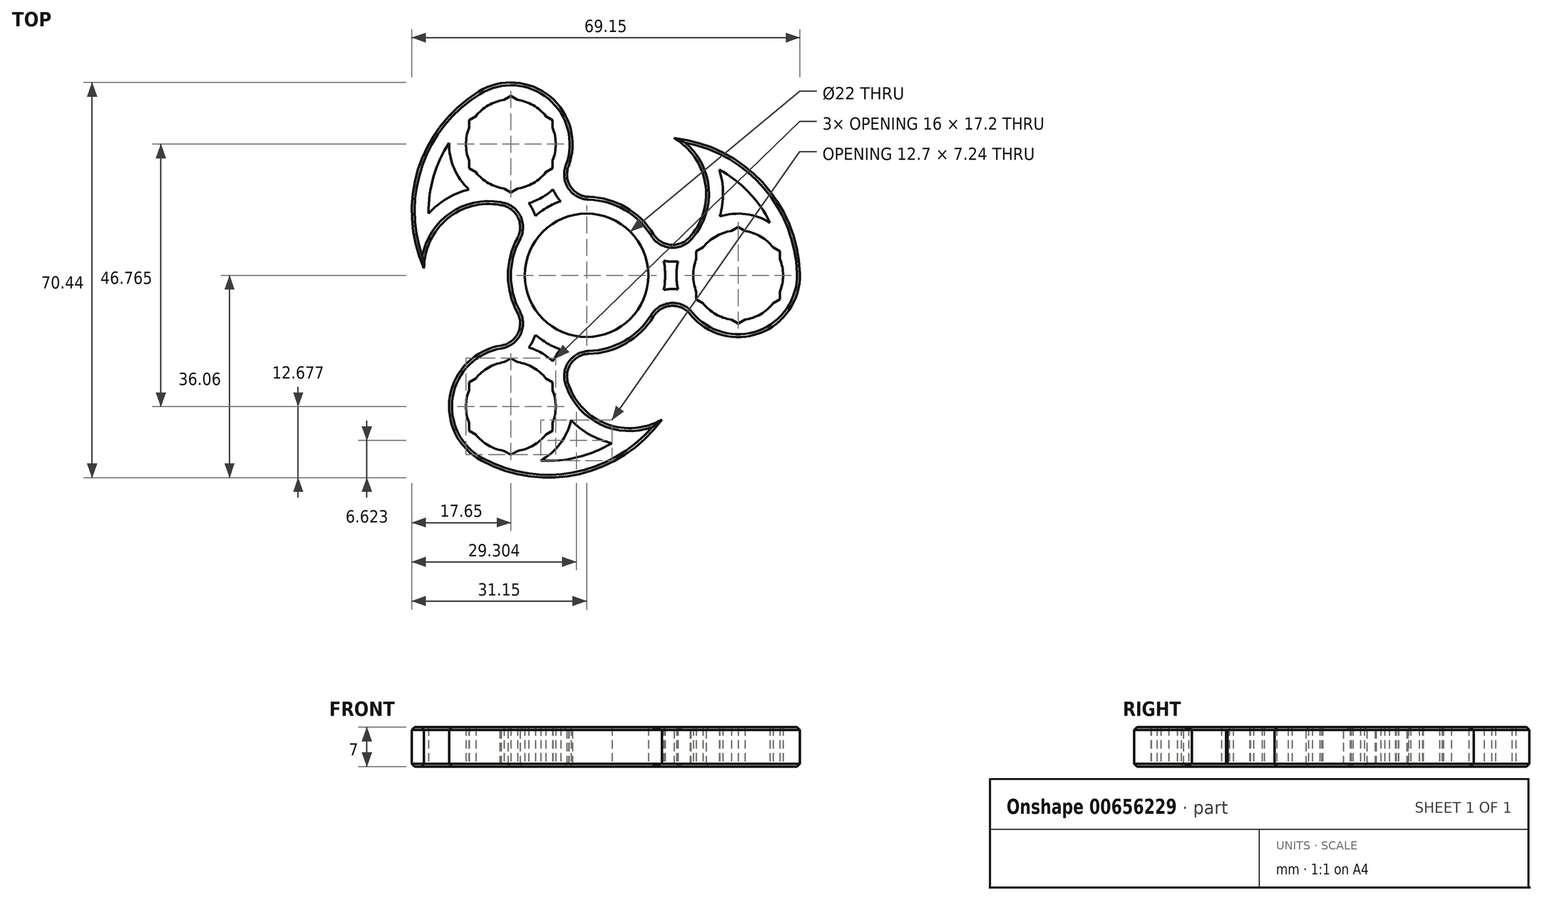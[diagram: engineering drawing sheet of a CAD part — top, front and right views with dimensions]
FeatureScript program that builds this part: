
annotation { "Feature Type Name" : "Feature", "Feature Type Description" : "" }
export const myFeature = defineFeature(function(context is Context, id is Id, definition is map)
    precondition{}
    {
        {
            var Q0;
            Q0=qCreatedBy(makeId("Top.planeOp"),FACE);
            var sketch = newSketch(context, id + "F0", { "sketchPlane" : qUnion([Q0])});
            skCircle(sketch, "E0", {"center": v(0, 0) * mm, "radius": 11 * mm});
            skCircle(sketch, "E1", {"center": v(0, 0) * mm, "radius": 27 * mm, "construction": true});
            skCircle(sketch, "E2", {"center": v(27, 0) * mm, "radius": 8 * mm});
            skArc(sketch, "E3.0", {"start": v(18.44, -6.91) * mm, "mid": v(30.82, -10.32) * mm, "end": v(38, 0.32) * mm});
            skCircle(sketch, "E4", {"center": v(0, 0) * mm, "radius": 29 * mm, "construction": true});
            skLineSegment(sketch, "E5", {"start": v(27, 0) * mm, "end": v(15.57, 24.46) * mm, "construction": true});
            skArc(sketch, "E6", {"start": v(38, 0.32) * mm, "mid": v(31.33, 16.6) * mm, "end": v(15.57, 24.46) * mm});
            skArc(sketch, "E7", {"start": v(18.6, 7.1) * mm, "mid": v(21.14, 16.48) * mm, "end": v(15.57, 24.46) * mm});
            skArc(sketch, "E8.0", {"start": v(13.75, -2.6) * mm, "mid": v(14, 0) * mm, "end": v(13.75, 2.6) * mm});
            skArc(sketch, "E9", {"start": v(11.93, 7.33) * mm, "mid": v(15.08, 5.44) * mm, "end": v(18.44, 6.91) * mm});
            skArc(sketch, "E10.0", {"start": v(13.75, 2.6) * mm, "mid": v(15.02, 2.44) * mm, "end": v(16.29, 2.5) * mm});
            skArc(sketch, "E11.MirrorCS", {"start": v(13.75, -2.6) * mm, "mid": v(15.02, -2.44) * mm, "end": v(16.29, -2.5) * mm});
            skArc(sketch, "E12.MirrorCS", {"start": v(11.93, -7.33) * mm, "mid": v(15.08, -5.44) * mm, "end": v(18.44, -6.91) * mm});
            skArc(sketch, "E13.trimOffspring", {"start": v(16.29, 2.5) * mm, "mid": v(16, 0) * mm, "end": v(16.29, -2.5) * mm});
            skArc(sketch, "E14.trimOffspring", {"start": v(11.93, 7.33) * mm, "mid": v(7, 12.12) * mm, "end": v(0.39, 14) * mm});
            skArc(sketch, "E15.0", {"start": v(32.7, 9.41) * mm, "mid": v(28.89, 14.82) * mm, "end": v(23.64, 18.85) * mm});
            skArc(sketch, "E16.0", {"start": v(23.74, 10.5) * mm, "mid": v(24.3, 14.69) * mm, "end": v(23.64, 18.85) * mm});
            skArc(sketch, "E17.trimOffspring", {"start": v(32.7, 9.41) * mm, "mid": v(28.34, 10.92) * mm, "end": v(23.74, 10.5) * mm});
            skArc(sketch, "E18.1.0", {"start": v(-24.5, 23.6) * mm, "mid": v(-23.62, 19.08) * mm, "end": v(-20.97, 15.3) * mm});
            skArc(sketch, "E18.1.1", {"start": v(-20.97, 15.3) * mm, "mid": v(-24.87, 13.7) * mm, "end": v(-28.15, 11.05) * mm});
            skArc(sketch, "E18.1.2", {"start": v(0.39, 14) * mm, "mid": v(-2.83, 15.77) * mm, "end": v(-3.23, 19.43) * mm});
            skArc(sketch, "E18.1.3", {"start": v(-4.62, 13.22) * mm, "mid": v(-5.4, 14.22) * mm, "end": v(-5.98, 15.35) * mm});
            skArc(sketch, "E18.1.4", {"start": v(-9.14, 10.6) * mm, "mid": v(-9.62, 11.79) * mm, "end": v(-10.3, 12.86) * mm});
            skArc(sketch, "E18.1.5", {"start": v(-12.31, 6.66) * mm, "mid": v(-12.25, 10.34) * mm, "end": v(-15.2, 12.52) * mm});
            skArc(sketch, "E18.1.6", {"start": v(-4.62, 13.22) * mm, "mid": v(-7, 12.12) * mm, "end": v(-9.14, 10.6) * mm});
            skArc(sketch, "E18.1.7", {"start": v(-15.44, 12.56) * mm, "mid": v(-24.84, 10.06) * mm, "end": v(-28.97, 1.26) * mm});
            skArc(sketch, "E18.1.8", {"start": v(-19.27, 32.75) * mm, "mid": v(-30.04, 18.83) * mm, "end": v(-28.97, 1.26) * mm});
            skArc(sketch, "E18.1.9", {"start": v(-3.23, 19.43) * mm, "mid": v(-6.47, 31.85) * mm, "end": v(-19.27, 32.75) * mm});
            skCircle(sketch, "E18.1.10", {"center": v(-13.5, 23.38) * mm, "radius": 8 * mm});
            skArc(sketch, "E18.1.11", {"start": v(-24.5, 23.6) * mm, "mid": v(-27.28, 17.6) * mm, "end": v(-28.15, 11.05) * mm});
            skArc(sketch, "E18.1.12", {"start": v(-10.3, 12.86) * mm, "mid": v(-8, 13.86) * mm, "end": v(-5.98, 15.35) * mm});
            skArc(sketch, "E18.2.0", {"start": v(-8.2, -33.02) * mm, "mid": v(-4.71, -30) * mm, "end": v(-2.77, -25.81) * mm});
            skArc(sketch, "E18.2.1", {"start": v(-2.77, -25.81) * mm, "mid": v(0.57, -28.4) * mm, "end": v(4.5, -29.9) * mm});
            skArc(sketch, "E18.2.2", {"start": v(-12.31, -6.66) * mm, "mid": v(-12.25, -10.34) * mm, "end": v(-15.2, -12.52) * mm});
            skArc(sketch, "E18.2.3", {"start": v(-9.14, -10.6) * mm, "mid": v(-9.62, -11.79) * mm, "end": v(-10.3, -12.86) * mm});
            skArc(sketch, "E18.2.4", {"start": v(-4.62, -13.22) * mm, "mid": v(-5.4, -14.22) * mm, "end": v(-5.98, -15.35) * mm});
            skArc(sketch, "E18.2.5", {"start": v(0.39, -14) * mm, "mid": v(-2.83, -15.77) * mm, "end": v(-3.23, -19.43) * mm});
            skArc(sketch, "E18.2.6", {"start": v(-9.14, -10.6) * mm, "mid": v(-7, -12.12) * mm, "end": v(-4.62, -13.22) * mm});
            skArc(sketch, "E18.2.7", {"start": v(-3.15, -19.65) * mm, "mid": v(3.7, -26.55) * mm, "end": v(13.4, -25.72) * mm});
            skArc(sketch, "E18.2.8", {"start": v(-18.72, -33.06) * mm, "mid": v(-1.28, -35.43) * mm, "end": v(13.4, -25.72) * mm});
            skArc(sketch, "E18.2.9", {"start": v(-15.2, -12.52) * mm, "mid": v(-24.34, -21.53) * mm, "end": v(-18.72, -33.06) * mm});
            skCircle(sketch, "E18.2.10", {"center": v(-13.5, -23.38) * mm, "radius": 8 * mm});
            skArc(sketch, "E18.2.11", {"start": v(-8.2, -33.02) * mm, "mid": v(-1.6, -32.43) * mm, "end": v(4.5, -29.9) * mm});
            skArc(sketch, "E18.2.12", {"start": v(-5.98, -15.35) * mm, "mid": v(-8, -13.86) * mm, "end": v(-10.3, -12.86) * mm});
            skArc(sketch, "E19.trimOffspring", {"start": v(-12.31, 6.66) * mm, "mid": v(-14, 0) * mm, "end": v(-12.31, -6.66) * mm});
            skArc(sketch, "E20.trimOffspring", {"start": v(0.39, -14) * mm, "mid": v(7, -12.12) * mm, "end": v(11.93, -7.33) * mm});
            skLineSegment(sketch, "E21", {"start": v(18.44, 6.91) * mm, "end": v(18.6, 7.1) * mm});
            skLineSegment(sketch, "E22", {"start": v(-15.2, 12.52) * mm, "end": v(-15.44, 12.56) * mm});
            skLineSegment(sketch, "E23", {"start": v(-3.15, -19.65) * mm, "end": v(-3.23, -19.43) * mm});
            skCircle(sketch, "E24.cCircle", {"center": v(27, 0) * mm, "radius": 8.6 * mm, "construction": true});
            skLineSegment(sketch, "E24.0", {"start": v(34.45, 4.3) * mm, "end": v(34.45, -4.3) * mm});
            skLineSegment(sketch, "E24.1", {"start": v(34.45, -4.3) * mm, "end": v(27, -8.6) * mm});
            skLineSegment(sketch, "E24.2", {"start": v(27, -8.6) * mm, "end": v(19.55, -4.3) * mm});
            skLineSegment(sketch, "E24.3", {"start": v(19.55, -4.3) * mm, "end": v(19.55, 4.3) * mm});
            skLineSegment(sketch, "E24.4", {"start": v(19.55, 4.3) * mm, "end": v(27, 8.6) * mm});
            skLineSegment(sketch, "E24.5", {"start": v(27, 8.6) * mm, "end": v(34.45, 4.3) * mm});
            skLineSegment(sketch, "E25.1.0", {"start": v(-13.5, 31.98) * mm, "end": v(-6.05, 27.68) * mm});
            skLineSegment(sketch, "E25.1.1", {"start": v(-20.95, 27.68) * mm, "end": v(-13.5, 31.98) * mm});
            skLineSegment(sketch, "E25.1.2", {"start": v(-20.95, 19.08) * mm, "end": v(-20.95, 27.68) * mm});
            skLineSegment(sketch, "E25.1.3", {"start": v(-13.5, 14.78) * mm, "end": v(-20.95, 19.08) * mm});
            skLineSegment(sketch, "E25.1.4", {"start": v(-6.05, 19.08) * mm, "end": v(-13.5, 14.78) * mm});
            skLineSegment(sketch, "E25.1.5", {"start": v(-6.05, 27.68) * mm, "end": v(-6.05, 19.08) * mm});
            skLineSegment(sketch, "E25.2.0", {"start": v(-20.95, -27.68) * mm, "end": v(-20.95, -19.08) * mm});
            skLineSegment(sketch, "E25.2.1", {"start": v(-13.5, -31.98) * mm, "end": v(-20.95, -27.68) * mm});
            skLineSegment(sketch, "E25.2.2", {"start": v(-6.05, -27.68) * mm, "end": v(-13.5, -31.98) * mm});
            skLineSegment(sketch, "E25.2.3", {"start": v(-6.05, -19.08) * mm, "end": v(-6.05, -27.68) * mm});
            skLineSegment(sketch, "E25.2.4", {"start": v(-13.5, -14.78) * mm, "end": v(-6.05, -19.08) * mm});
            skLineSegment(sketch, "E25.2.5", {"start": v(-20.95, -19.08) * mm, "end": v(-13.5, -14.78) * mm});
            skSolve(sketch);
        }
        {
            var Q0;
            Q0=makeQuery(id+"F0.imprint","IMPRINT",FACE,{"disambiguationData":[TD([[makeQuery(id+"F0.imprint","IMPRINT",EDGE,{"derivedFrom":sQuery(id+"F0.wireOp",EDGE,"E0")}),-1.0]])]});
            extrude(context, id + "F1", {"entities" : qUnion([Q0]), "endBound" : BoundingType.SYMMETRIC, "depth" : 7 * mm, "offsetDistance" : 25 * mm});
        }
        {
            var Q0;
            Q0=makeQuery(id+"F1.opExtrude","CAP_EDGE",EDGE,{"disambiguationData":[OSD([sQuery(id+"F0.wireOp",EDGE,"E20.trimOffspring")])],"isStart":true});
            var Q1;
            Q1=makeQuery(id+"F1.opExtrude","CAP_EDGE",EDGE,{"disambiguationData":[OSD([sQuery(id+"F0.wireOp",EDGE,"E18.2.9")])],"isStart":true});
            var Q2;
            Q2=makeQuery(id+"F1.opExtrude","CAP_EDGE",EDGE,{"disambiguationData":[OSD([sQuery(id+"F0.wireOp",EDGE,"E18.2.7")])],"isStart":true});
            var Q3;
            Q3=makeQuery(id+"F1.opExtrude","CAP_EDGE",EDGE,{"disambiguationData":[OSD([sQuery(id+"F0.wireOp",EDGE,"E18.1.7")])],"isStart":true});
            var Q4;
            Q4=makeQuery(id+"F1.opExtrude","CAP_EDGE",EDGE,{"disambiguationData":[OSD([sQuery(id+"F0.wireOp",EDGE,"E18.1.8")])],"isStart":true});
            var Q5;
            Q5=makeQuery(id+"F1.opExtrude","CAP_EDGE",EDGE,{"disambiguationData":[OSD([sQuery(id+"F0.wireOp",EDGE,"E7")])],"isStart":true});
            var Q6;
            Q6=makeQuery(id+"F1.opExtrude","CAP_EDGE",EDGE,{"disambiguationData":[OSD([sQuery(id+"F0.wireOp",EDGE,"E7")])],"isStart":false});
            var Q7;
            Q7=makeQuery(id+"F1.opExtrude","CAP_EDGE",EDGE,{"disambiguationData":[OSD([sQuery(id+"F0.wireOp",EDGE,"E14.trimOffspring")])],"isStart":false});
            var Q8;
            Q8=makeQuery(id+"F1.opExtrude","CAP_EDGE",EDGE,{"disambiguationData":[OSD([sQuery(id+"F0.wireOp",EDGE,"E6")])],"isStart":false});
            var Q9;
            Q9=makeQuery(id+"F1.opExtrude","CAP_EDGE",EDGE,{"disambiguationData":[OSD([sQuery(id+"F0.wireOp",EDGE,"E18.2.7")])],"isStart":false});
            var Q10;
            Q10=makeQuery(id+"F1.opExtrude","CAP_EDGE",EDGE,{"disambiguationData":[OSD([sQuery(id+"F0.wireOp",EDGE,"E18.2.8")])],"isStart":false});
            var Q11;
            Q11=makeQuery(id+"F1.opExtrude","CAP_EDGE",EDGE,{"disambiguationData":[OSD([sQuery(id+"F0.wireOp",EDGE,"E18.1.7")])],"isStart":false});
            chamfer(context, id + "F2", {"entities" : qUnion([Q0, Q1, Q2, Q3, Q4, Q5, Q6, Q7, Q8, Q9, Q10, Q11]), "width" : 0.5 * mm, "tangentPropagation" : true});
        }
    });
